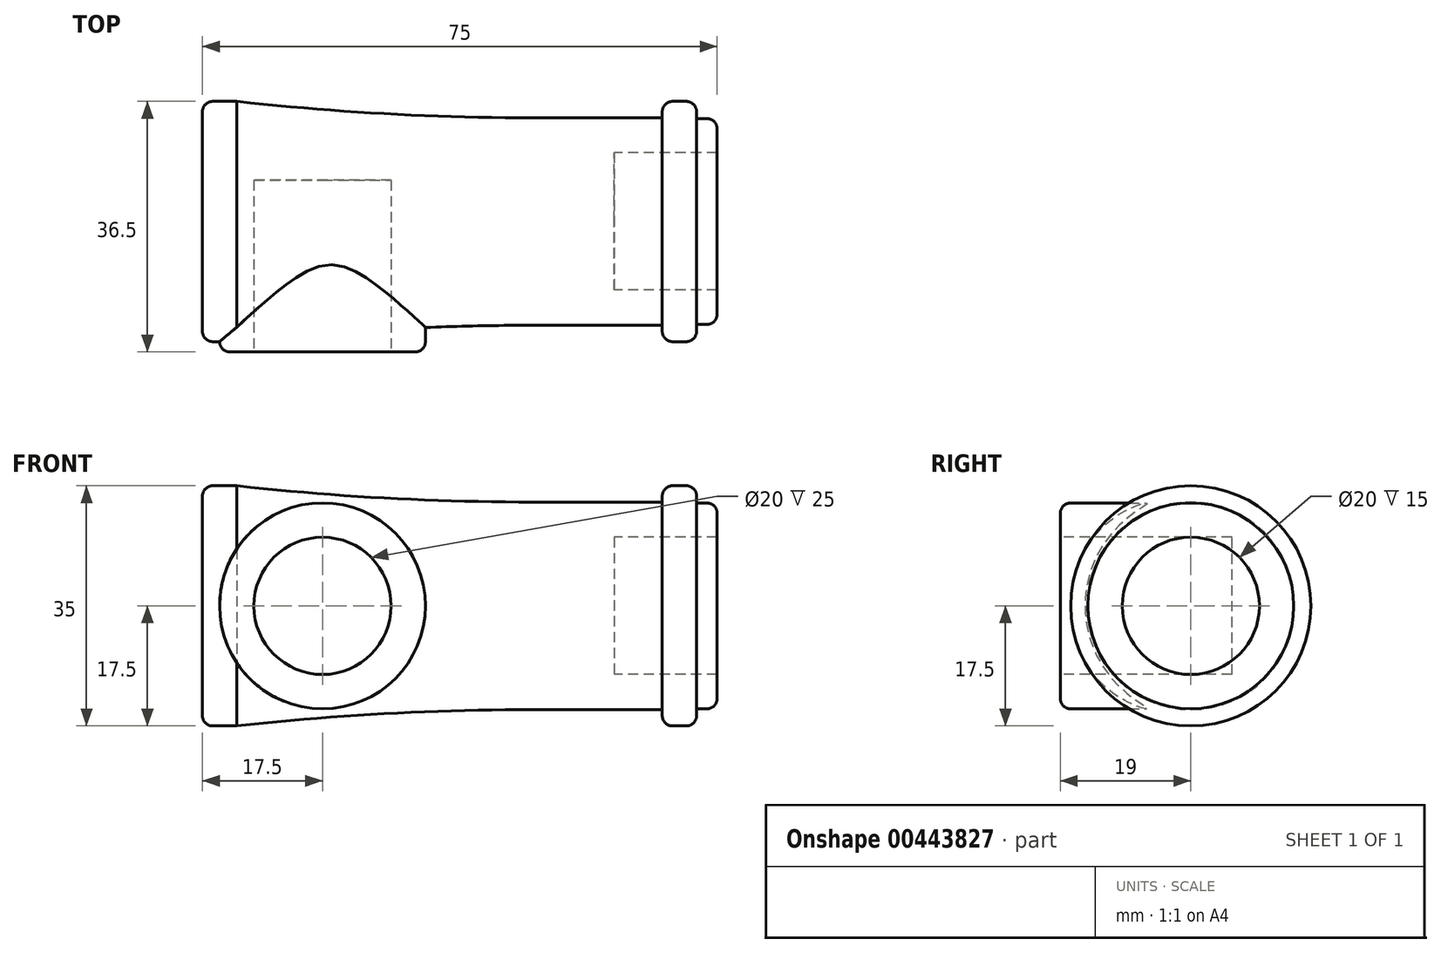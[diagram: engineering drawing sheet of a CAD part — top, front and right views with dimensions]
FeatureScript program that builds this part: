
annotation { "Feature Type Name" : "Feature", "Feature Type Description" : "" }
export const myFeature = defineFeature(function(context is Context, id is Id, definition is map)
    precondition{}
    {
        {
            var Q0;
            Q0=qCreatedBy(makeId("Front.planeOp"),FACE);
            var sketch = newSketch(context, id + "F0", { "sketchPlane" : qUnion([Q0])});
            skLineSegment(sketch, "E0", {"start": v(0, 0) * mm, "end": v(60, 0) * mm});
            skLineSegment(sketch, "E1", {"start": v(60, 0) * mm, "end": v(60, 10) * mm});
            skLineSegment(sketch, "E2", {"start": v(60, 10) * mm, "end": v(75, 10) * mm});
            skLineSegment(sketch, "E3", {"start": v(75, 10) * mm, "end": v(75, 15) * mm});
            skLineSegment(sketch, "E4", {"start": v(75, 15) * mm, "end": v(72, 15) * mm});
            skLineSegment(sketch, "E5", {"start": v(72, 15) * mm, "end": v(72, 17.5) * mm});
            skLineSegment(sketch, "E6", {"start": v(72, 17.5) * mm, "end": v(67, 17.5) * mm});
            skLineSegment(sketch, "E7", {"start": v(67, 17.5) * mm, "end": v(67, 15.12) * mm});
            skLineSegment(sketch, "E8", {"start": v(67, 15.12) * mm, "end": v(50, 15.12) * mm});
            skLineSegment(sketch, "E9", {"start": v(0, 0) * mm, "end": v(0, 17.5) * mm});
            skLineSegment(sketch, "E10", {"start": v(0, 17.5) * mm, "end": v(5, 17.5) * mm});
            skArc(sketch, "E11", {"start": v(5, 17.5) * mm, "mid": v(27.47, 15.67) * mm, "end": v(50, 15.12) * mm});
            skSolve(sketch);
        }
        {
            var Q0;
            Q0=makeQuery(id+"F0.imprint","IMPRINT",FACE,{"disambiguationData":[TD([[makeQuery(id+"F0.imprint","IMPRINT",EDGE,{"derivedFrom":sQuery(id+"F0.wireOp",EDGE,"E0")}),1.0]])]});
            var Q1;
            Q1=sQuery(id+"F0.wireOp",EDGE,"E0");
            revolve(context, id + "F1", {"entities" : qUnion([Q0]), "axis" : qUnion([Q1]), "revolveType" : RevolveType.FULL});
        }
        {
            var Q0;
            Q0=qCreatedBy(makeId("Front.planeOp"),FACE);
            var sketch = newSketch(context, id + "F2", { "sketchPlane" : qUnion([Q0])});
            skCircle(sketch, "E12", {"center": v(17.5, 0) * mm, "radius": 15 * mm});
            skSolve(sketch);
        }
        {
            var Q0;
            Q0 = qSketchRegion(id + "F2", true);
            extrude(context, id + "F3", {"entities" : qUnion([Q0]), "operationType" : NewBodyOperationType.ADD, "depth" : 19 * mm});
        }
        {
            var Q0;
            Q0=makeQuery(id+"F3.opExtrude","CAP_FACE",FACE,{"disambiguationData":[OSD([sQuery(id+"F2.wireOp",EDGE,"E12")])],"isStart":false});
            var sketch = newSketch(context, id + "F4", { "sketchPlane" : qUnion([Q0])});
            skCircle(sketch, "E13", {"center": v(17.5, 0) * mm, "radius": 10 * mm});
            skSolve(sketch);
        }
        {
            var Q0;
            Q0 = qSketchRegion(id + "F4", true);
            extrude(context, id + "F5", {"entities" : qUnion([Q0]), "operationType" : NewBodyOperationType.REMOVE, "oppositeDirection" : true, "depth" : 25 * mm});
        }
        {
            var Q0;
            Q0=makeQuery(id+"F1.opRevolve","SWEPT_EDGE",EDGE,{"disambiguationData":[OSD([sQuery(id+"F0.wireOp",EDGE,"E9"),sQuery(id+"F0.wireOp",EDGE,"E10")])]});
            var Q1;
            Q1=makeQuery(id+"F3.opExtrude","CAP_EDGE",EDGE,{"disambiguationData":[OSD([sQuery(id+"F2.wireOp",EDGE,"E12")])],"isStart":false});
            var Q2;
            Q2=makeQuery(id+"F1.opRevolve","SWEPT_EDGE",EDGE,{"disambiguationData":[OSD([sQuery(id+"F0.wireOp",EDGE,"E6"),sQuery(id+"F0.wireOp",EDGE,"E7")])]});
            var Q3;
            Q3=makeQuery(id+"F1.opRevolve","SWEPT_EDGE",EDGE,{"disambiguationData":[OSD([sQuery(id+"F0.wireOp",EDGE,"E5"),sQuery(id+"F0.wireOp",EDGE,"E6")])]});
            var Q4;
            Q4=makeQuery(id+"F1.opRevolve","SWEPT_EDGE",EDGE,{"disambiguationData":[OSD([sQuery(id+"F0.wireOp",EDGE,"E3"),sQuery(id+"F0.wireOp",EDGE,"E4")])]});
            fillet(context, id + "F6", {"entities" : qUnion([Q0, Q1, Q2, Q3, Q4]), "radius" : 1.5 * mm, "tangentPropagation" : true, "allowEdgeOverflow" : false});
        }
    });
